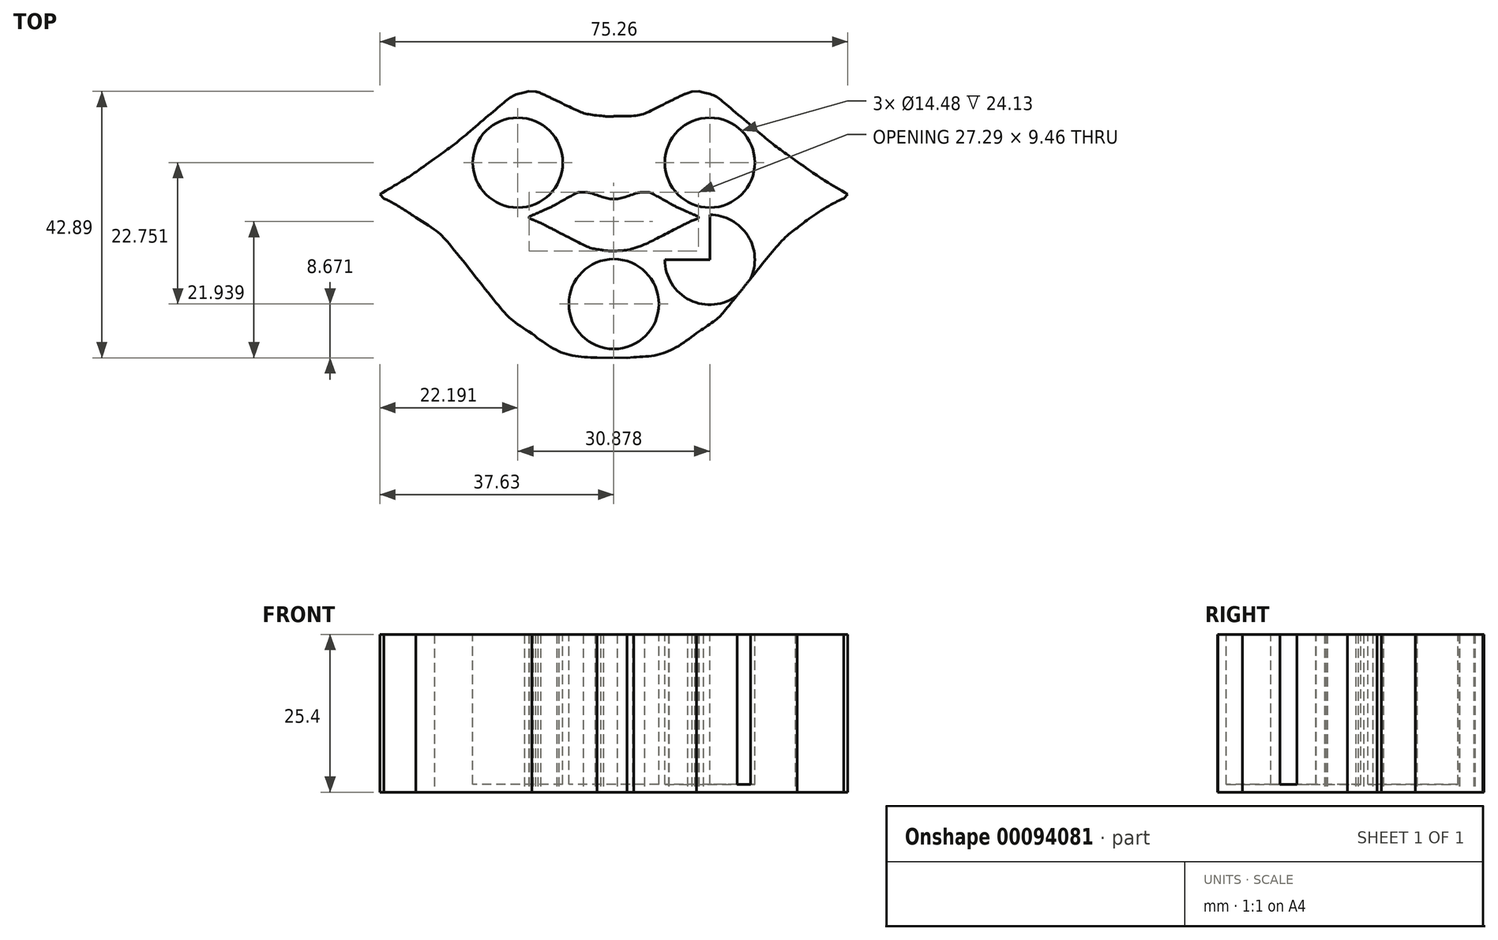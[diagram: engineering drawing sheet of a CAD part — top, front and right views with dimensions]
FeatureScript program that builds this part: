
annotation { "Feature Type Name" : "Feature", "Feature Type Description" : "" }
export const myFeature = defineFeature(function(context is Context, id is Id, definition is map)
    precondition{}
    {
        {
            var Q0;
            Q0=qCreatedBy(makeId("Top.planeOp"),FACE);
            var sketch = newSketch(context, id + "F0", { "sketchPlane" : qUnion([Q0])});
            skFitSpline(sketch, "E0", {"points": [v(-5.79, -23.43) * mm, v(-9.7, -22.6) * mm, v(-14.21, -19.9) * mm, v(-17.72, -16.3) * mm]});
            skFitSpline(sketch, "E1", {"points": [v(-17.72, -16.3) * mm, v(-19.37, -14.6) * mm, v(-19.96, -13.9) * mm, v(-22.42, -10.84) * mm]});
            skFitSpline(sketch, "E2", {"points": [v(-22.42, -10.84) * mm, v(-25.94, -6.44) * mm, v(-27.82, -4.4) * mm, v(-29.91, -2.76) * mm]});
            skFitSpline(sketch, "E3", {"points": [v(-29.91, -2.76) * mm, v(-31.51, -1.5) * mm, v(-35.93, 1.25) * mm, v(-37.43, 1.91) * mm]});
            skFitSpline(sketch, "E4", {"points": [v(-37.43, 1.91) * mm, v(-37.97, 2.15) * mm, v(-38.1, 2.27) * mm, v(-38.1, 2.52) * mm]});
            skFitSpline(sketch, "E5", {"points": [v(-38.1, 2.52) * mm, v(-38.1, 2.77) * mm, v(-37.87, 2.96) * mm, v(-36.73, 3.63) * mm]});
            skFitSpline(sketch, "E6", {"points": [v(-36.73, 3.63) * mm, v(-32.2, 6.28) * mm, v(-26.83, 10.13) * mm, v(-22.5, 13.82) * mm]});
            skFitSpline(sketch, "E7", {"points": [v(-22.5, 13.82) * mm, v(-19.29, 16.56) * mm, v(-18.61, 17.1) * mm, v(-17.4, 17.92) * mm]});
            skFitSpline(sketch, "E8", {"points": [v(-17.4, 17.92) * mm, v(-15.92, 18.91) * mm, v(-15.04, 19.3) * mm, v(-14.29, 19.3) * mm]});
            skFitSpline(sketch, "E9", {"points": [v(-14.37, 19.1) * mm, v(-15.97, 18.67) * mm, v(-17.57, 17.59) * mm, v(-21.4, 14.33) * mm]});
            skFitSpline(sketch, "E10", {"points": [v(-21.4, 14.33) * mm, v(-24.87, 11.4) * mm, v(-26.2, 10.35) * mm, v(-28.87, 8.44) * mm]});
            skFitSpline(sketch, "E11", {"points": [v(-28.87, 8.44) * mm, v(-32.22, 6.05) * mm, v(-33.92, 4.94) * mm, v(-37.63, 2.73) * mm]});
            skLineSegment(sketch, "E12", {"start": v(-14.29, 19.3) * mm, "end": v(-13.7, 19.28) * mm});
            skLineSegment(sketch, "E13", {"start": v(-13.7, 19.28) * mm, "end": v(-14.37, 19.1) * mm});
            skLineSegment(sketch, "E14", {"start": v(-14.37, 19.1) * mm, "end": v(-14.29, 19.3) * mm});
            skFitSpline(sketch, "E15", {"points": [v(-37.01, 2.05) * mm, v(-35.86, 1.5) * mm, v(-33.73, 0.24) * mm, v(-31.86, -1) * mm]});
            skFitSpline(sketch, "E16", {"points": [v(-31.86, -1) * mm, v(-28.39, -3.31) * mm, v(-26.8, -4.9) * mm, v(-22.17, -10.65) * mm]});
            skFitSpline(sketch, "E17", {"points": [v(-22.17, -10.65) * mm, v(-17.88, -15.97) * mm, v(-16.31, -17.55) * mm, v(-13.19, -19.7) * mm]});
            skFitSpline(sketch, "E18", {"points": [v(-13.19, -19.7) * mm, v(-9.72, -22.1) * mm, v(-6.52, -23.27) * mm, v(-2.68, -23.55) * mm]});
            skFitSpline(sketch, "E19", {"points": [v(-2.68, -23.55) * mm, v(-2.36, -23.58) * mm, v(-2.73, -23.6) * mm, v(-3.5, -23.6) * mm]});
            skFitSpline(sketch, "E20", {"points": [v(-3.5, -23.6) * mm, v(-4.3, -23.62) * mm, v(-5.28, -23.54) * mm, v(-5.79, -23.43) * mm]});
            skLineSegment(sketch, "E21", {"start": v(-37.63, 2.73) * mm, "end": v(-38, 2.52) * mm});
            skLineSegment(sketch, "E22", {"start": v(-38, 2.52) * mm, "end": v(-37.01, 2.05) * mm});
            skLineSegment(sketch, "E23", {"start": v(-37.01, 2.05) * mm, "end": v(-37.63, 2.73) * mm});
            skFitSpline(sketch, "E24", {"points": [v(3.19, -23.5) * mm, v(6.82, -23.15) * mm, v(9.98, -21.94) * mm, v(13.32, -19.62) * mm]});
            skFitSpline(sketch, "E25", {"points": [v(13.32, -19.62) * mm, v(16.41, -17.47) * mm, v(17.9, -15.94) * mm, v(22.64, -10.07) * mm]});
            skFitSpline(sketch, "E26", {"points": [v(22.64, -10.07) * mm, v(25.5, -6.52) * mm, v(27.9, -3.93) * mm, v(29.47, -2.7) * mm]});
            skFitSpline(sketch, "E27", {"points": [v(29.47, -2.7) * mm, v(31.47, -1.16) * mm, v(35.15, 1.17) * mm, v(37.01, 2.05) * mm]});
            skFitSpline(sketch, "E28", {"points": [v(37.63, 2.73) * mm, v(33.92, 4.94) * mm, v(32.57, 5.82) * mm, v(29.18, 8.22) * mm]});
            skFitSpline(sketch, "E29", {"points": [v(29.18, 8.22) * mm, v(26.56, 10.07) * mm, v(24.5, 11.69) * mm, v(21.79, 14) * mm]});
            skFitSpline(sketch, "E30", {"points": [v(21.79, 14) * mm, v(17.56, 17.62) * mm, v(16.07, 18.64) * mm, v(14.37, 19.1) * mm]});
            skLineSegment(sketch, "E31", {"start": v(37.01, 2.05) * mm, "end": v(38, 2.52) * mm});
            skLineSegment(sketch, "E32", {"start": v(38, 2.52) * mm, "end": v(37.63, 2.73) * mm});
            skLineSegment(sketch, "E33", {"start": v(37.63, 2.73) * mm, "end": v(37.01, 2.05) * mm});
            skFitSpline(sketch, "E34", {"points": [v(14.29, 19.3) * mm, v(15.04, 19.3) * mm, v(15.92, 18.91) * mm, v(17.4, 17.92) * mm]});
            skFitSpline(sketch, "E35", {"points": [v(17.4, 17.92) * mm, v(18.6, 17.1) * mm, v(19.26, 16.58) * mm, v(22.45, 13.86) * mm]});
            skFitSpline(sketch, "E36", {"points": [v(22.45, 13.86) * mm, v(23.53, 12.94) * mm, v(24.85, 11.85) * mm, v(25.37, 11.44) * mm]});
            skFitSpline(sketch, "E37", {"points": [v(25.37, 11.44) * mm, v(28.39, 9.04) * mm, v(33.59, 5.47) * mm, v(36.64, 3.68) * mm]});
            skFitSpline(sketch, "E38", {"points": [v(36.64, 3.68) * mm, v(37.86, 2.96) * mm, v(38.1, 2.77) * mm, v(38.1, 2.52) * mm]});
            skFitSpline(sketch, "E39", {"points": [v(38.1, 2.52) * mm, v(38.1, 2.27) * mm, v(37.97, 2.15) * mm, v(37.43, 1.91) * mm]});
            skFitSpline(sketch, "E40", {"points": [v(37.43, 1.91) * mm, v(35.93, 1.25) * mm, v(31.51, -1.5) * mm, v(29.91, -2.76) * mm]});
            skFitSpline(sketch, "E41", {"points": [v(29.91, -2.76) * mm, v(27.82, -4.4) * mm, v(25.94, -6.44) * mm, v(22.42, -10.84) * mm]});
            skFitSpline(sketch, "E42", {"points": [v(22.42, -10.84) * mm, v(19.96, -13.9) * mm, v(19.37, -14.6) * mm, v(17.72, -16.3) * mm]});
            skFitSpline(sketch, "E43", {"points": [v(17.72, -16.3) * mm, v(13.36, -20.77) * mm, v(7.7, -23.68) * mm, v(3.46, -23.63) * mm]});
            skLineSegment(sketch, "E44", {"start": v(14.37, 19.1) * mm, "end": v(13.7, 19.28) * mm});
            skLineSegment(sketch, "E45", {"start": v(13.7, 19.28) * mm, "end": v(14.29, 19.3) * mm});
            skLineSegment(sketch, "E46", {"start": v(14.29, 19.3) * mm, "end": v(14.37, 19.1) * mm});
            skFitSpline(sketch, "E47", {"points": [v(-2.1, -6.2) * mm, v(-3.6, -5.95) * mm, v(-5.15, -5.3) * mm, v(-9.5, -3.07) * mm]});
            skFitSpline(sketch, "E48", {"points": [v(-9.5, -3.07) * mm, v(-11.03, -2.28) * mm, v(-12.6, -1.53) * mm, v(-12.97, -1.4) * mm]});
            skFitSpline(sketch, "E49", {"points": [v(-12.97, -1.4) * mm, v(-13.33, -1.27) * mm, v(-13.63, -1.1) * mm, v(-13.63, -1.02) * mm]});
            skFitSpline(sketch, "E50", {"points": [v(-13.63, -1.02) * mm, v(-13.63, -0.95) * mm, v(-12.81, -0.52) * mm, v(-11.81, -0.09) * mm]});
            skFitSpline(sketch, "E51", {"points": [v(-11.81, -0.09) * mm, v(-10.81, 0.35) * mm, v(-9.48, 1) * mm, v(-8.85, 1.35) * mm]});
            skFitSpline(sketch, "E52", {"points": [v(-8.85, 1.35) * mm, v(-6.3, 2.79) * mm, v(-5.72, 3.03) * mm, v(-4.9, 3.04) * mm]});
            skFitSpline(sketch, "E53", {"points": [v(-4.9, 3.04) * mm, v(-4.4, 3.05) * mm, v(-3.75, 2.93) * mm, v(-3, 2.7) * mm]});
            skFitSpline(sketch, "E54", {"points": [v(-3, 2.7) * mm, v(-0.82, 2.02) * mm, v(0.82, 2.02) * mm, v(3, 2.7) * mm]});
            skFitSpline(sketch, "E55", {"points": [v(3, 2.7) * mm, v(3.75, 2.93) * mm, v(4.4, 3.05) * mm, v(4.9, 3.04) * mm]});
            skFitSpline(sketch, "E56", {"points": [v(4.9, 3.04) * mm, v(5.72, 3.03) * mm, v(6.3, 2.79) * mm, v(8.85, 1.35) * mm]});
            skFitSpline(sketch, "E57", {"points": [v(8.85, 1.35) * mm, v(9.48, 1) * mm, v(10.81, 0.35) * mm, v(11.81, -0.09) * mm]});
            skFitSpline(sketch, "E58", {"points": [v(11.81, -0.09) * mm, v(12.81, -0.52) * mm, v(13.63, -0.95) * mm, v(13.63, -1.02) * mm]});
            skFitSpline(sketch, "E59", {"points": [v(13.63, -1.02) * mm, v(13.63, -1.1) * mm, v(13.33, -1.27) * mm, v(12.97, -1.4) * mm]});
            skFitSpline(sketch, "E60", {"points": [v(12.97, -1.4) * mm, v(12.6, -1.53) * mm, v(11.1, -2.25) * mm, v(9.62, -3.01) * mm]});
            skFitSpline(sketch, "E61", {"points": [v(9.62, -3.01) * mm, v(6.47, -4.63) * mm, v(4.34, -5.6) * mm, v(3.19, -5.95) * mm]});
            skFitSpline(sketch, "E62", {"points": [v(3.19, -5.95) * mm, v(2.26, -6.23) * mm, v(-0.96, -6.38) * mm, v(-2.1, -6.2) * mm]});
            skLineSegment(sketch, "E63", {"start": v(3.46, -23.63) * mm, "end": v(2.1, -23.6) * mm});
            skLineSegment(sketch, "E64", {"start": v(2.1, -23.6) * mm, "end": v(3.19, -23.5) * mm});
            skLineSegment(sketch, "E65", {"start": v(3.19, -23.5) * mm, "end": v(3.46, -23.63) * mm});
            skFitSpline(sketch, "E66", {"points": [v(2.79, -5.72) * mm, v(4.05, -5.4) * mm, v(6.73, -4.18) * mm, v(10.4, -2.25) * mm]});
            skFitSpline(sketch, "E67", {"points": [v(10.4, -2.25) * mm, v(11.2, -1.83) * mm, v(12.13, -1.38) * mm, v(12.49, -1.25) * mm]});
            skFitSpline(sketch, "E68", {"points": [v(12.27, -0.64) * mm, v(11.26, -0.22) * mm, v(8.41, 1.2) * mm, v(6.94, 2.03) * mm]});
            skFitSpline(sketch, "E69", {"points": [v(6.94, 2.03) * mm, v(6.38, 2.34) * mm, v(5.64, 2.66) * mm, v(5.29, 2.74) * mm]});
            skFitSpline(sketch, "E70", {"points": [v(5.29, 2.74) * mm, v(4.7, 2.87) * mm, v(4.53, 2.84) * mm, v(3.19, 2.42) * mm]});
            skFitSpline(sketch, "E71", {"points": [v(3.19, 2.42) * mm, v(0.71, 1.65) * mm, v(-0.76, 1.67) * mm, v(-3.4, 2.5) * mm]});
            skFitSpline(sketch, "E72", {"points": [v(-3.4, 2.5) * mm, v(-4.53, 2.84) * mm, v(-4.71, 2.87) * mm, v(-5.29, 2.74) * mm]});
            skFitSpline(sketch, "E73", {"points": [v(-5.29, 2.74) * mm, v(-5.64, 2.66) * mm, v(-6.38, 2.34) * mm, v(-6.94, 2.03) * mm]});
            skFitSpline(sketch, "E74", {"points": [v(-6.94, 2.03) * mm, v(-8.4, 1.21) * mm, v(-11.26, -0.22) * mm, v(-12.26, -0.64) * mm]});
            skLineSegment(sketch, "E75", {"start": v(12.49, -1.25) * mm, "end": v(13.14, -1) * mm});
            skLineSegment(sketch, "E76", {"start": v(13.14, -1) * mm, "end": v(12.27, -0.64) * mm});
            skLineSegment(sketch, "E77", {"start": v(12.27, -0.64) * mm, "end": v(12.49, -1.25) * mm});
            skFitSpline(sketch, "E78", {"points": [v(-12.07, -1.43) * mm, v(-11.5, -1.66) * mm, v(-10.42, -2.2) * mm, v(-9.68, -2.6) * mm]});
            skFitSpline(sketch, "E79", {"points": [v(-9.68, -2.6) * mm, v(-8.03, -3.53) * mm, v(-4.52, -5.18) * mm, v(-3.45, -5.54) * mm]});
            skFitSpline(sketch, "E80", {"points": [v(-3.45, -5.54) * mm, v(-1.86, -6.08) * mm, v(1.03, -6.16) * mm, v(2.79, -5.72) * mm]});
            skLineSegment(sketch, "E81", {"start": v(-12.26, -0.64) * mm, "end": v(-13.12, -1) * mm});
            skLineSegment(sketch, "E82", {"start": v(-13.12, -1) * mm, "end": v(-12.07, -1.43) * mm});
            skLineSegment(sketch, "E83", {"start": v(-12.07, -1.43) * mm, "end": v(-12.26, -0.64) * mm});
            skFitSpline(sketch, "E84", {"points": [v(-1.66, 15.3) * mm, v(-4.2, 15.63) * mm, v(-5.72, 16.13) * mm, v(-9.17, 17.78) * mm]});
            skFitSpline(sketch, "E85", {"points": [v(-9.17, 17.78) * mm, v(-10.61, 18.47) * mm, v(-11.99, 19.09) * mm, v(-12.23, 19.16) * mm]});
            skFitSpline(sketch, "E86", {"points": [v(-12.23, 19.16) * mm, v(-12.66, 19.3) * mm, v(-12.65, 19.3) * mm, v(-12, 19.25) * mm]});
            skFitSpline(sketch, "E87", {"points": [v(-12, 19.25) * mm, v(-11.47, 19.22) * mm, v(-10.82, 18.96) * mm, v(-8.7, 17.92) * mm]});
            skFitSpline(sketch, "E88", {"points": [v(-8.7, 17.92) * mm, v(-4.8, 16.04) * mm, v(-3.13, 15.59) * mm, v(0.06, 15.6) * mm]});
            skFitSpline(sketch, "E89", {"points": [v(0.06, 15.6) * mm, v(3.18, 15.6) * mm, v(5.1, 16.12) * mm, v(8.92, 18) * mm]});
            skFitSpline(sketch, "E90", {"points": [v(8.92, 18) * mm, v(10.82, 18.93) * mm, v(11.55, 19.23) * mm, v(12.04, 19.26) * mm]});
            skFitSpline(sketch, "E91", {"points": [v(11.85, 19) * mm, v(11.4, 18.84) * mm, v(10.02, 18.2) * mm, v(8.8, 17.6) * mm]});
            skFitSpline(sketch, "E92", {"points": [v(8.8, 17.6) * mm, v(5.38, 15.9) * mm, v(3.44, 15.36) * mm, v(0.5, 15.29) * mm]});
            skFitSpline(sketch, "E93", {"points": [v(0.5, 15.29) * mm, v(-0.44, 15.26) * mm, v(-1.41, 15.27) * mm, v(-1.66, 15.3) * mm]});
            skLineSegment(sketch, "E94", {"start": v(12.04, 19.26) * mm, "end": v(12.68, 19.31) * mm});
            skLineSegment(sketch, "E95", {"start": v(12.68, 19.31) * mm, "end": v(11.85, 19) * mm});
            skLineSegment(sketch, "E96", {"start": v(11.85, 19) * mm, "end": v(12.04, 19.26) * mm});
            skLineSegment(sketch, "E97", {"start": v(-1.66, 15.3) * mm, "end": v(-1.66, 15.3) * mm});
            skLineSegment(sketch, "E98", {"start": v(-2.68, -23.55) * mm, "end": v(2.1, -23.6) * mm});
            skLineSegment(sketch, "E99", {"start": v(-14.29, 19.3) * mm, "end": v(-12, 19.25) * mm});
            skLineSegment(sketch, "E100", {"start": v(12.04, 19.26) * mm, "end": v(14.29, 19.3) * mm});
            skLineSegment(sketch, "E101", {"start": v(13.7, 19.28) * mm, "end": v(13.7, 19.28) * mm});
            skSolve(sketch);
        }
        {
            var Q0;
            {var subQ6=sQuery(id+"F0.wireOp",EDGE,"E9");Q0=makeQuery(id+"F0.imprint","IMPRINT",FACE,{"disambiguationData":[TD([[makeQuery(id+"F0.imprint","IMPRINT",EDGE,{"derivedFrom":subQ6}),1.0]])]});}
            extrude(context, id + "F1", {"entities" : qUnion([Q0]), "depth" : 25.4 * mm});
        }
        {
            var Q0;
            Q0=makeQuery(id+"F1.opExtrude","CAP_FACE",FACE,{"disambiguationData":[OSD([sQuery(id+"F0.wireOp",EDGE,"E9"),sQuery(id+"F0.wireOp",EDGE,"E10"),sQuery(id+"F0.wireOp",EDGE,"E11"),sQuery(id+"F0.wireOp",EDGE,"E13"),sQuery(id+"F0.wireOp",EDGE,"E15"),sQuery(id+"F0.wireOp",EDGE,"E16"),sQuery(id+"F0.wireOp",EDGE,"E17"),sQuery(id+"F0.wireOp",EDGE,"E18"),sQuery(id+"F0.wireOp",EDGE,"E23"),sQuery(id+"F0.wireOp",EDGE,"E24"),sQuery(id+"F0.wireOp",EDGE,"E25"),sQuery(id+"F0.wireOp",EDGE,"E26"),sQuery(id+"F0.wireOp",EDGE,"E27"),sQuery(id+"F0.wireOp",EDGE,"E28"),sQuery(id+"F0.wireOp",EDGE,"E29"),sQuery(id+"F0.wireOp",EDGE,"E30"),sQuery(id+"F0.wireOp",EDGE,"E33"),sQuery(id+"F0.wireOp",EDGE,"E44"),sQuery(id+"F0.wireOp",EDGE,"E47"),sQuery(id+"F0.wireOp",EDGE,"E48"),sQuery(id+"F0.wireOp",EDGE,"E49"),sQuery(id+"F0.wireOp",EDGE,"E50"),sQuery(id+"F0.wireOp",EDGE,"E51"),sQuery(id+"F0.wireOp",EDGE,"E52"),sQuery(id+"F0.wireOp",EDGE,"E53"),sQuery(id+"F0.wireOp",EDGE,"E54"),sQuery(id+"F0.wireOp",EDGE,"E55"),sQuery(id+"F0.wireOp",EDGE,"E56"),sQuery(id+"F0.wireOp",EDGE,"E57"),sQuery(id+"F0.wireOp",EDGE,"E58"),sQuery(id+"F0.wireOp",EDGE,"E59"),sQuery(id+"F0.wireOp",EDGE,"E60"),sQuery(id+"F0.wireOp",EDGE,"E61"),sQuery(id+"F0.wireOp",EDGE,"E62"),sQuery(id+"F0.wireOp",EDGE,"E64"),sQuery(id+"F0.wireOp",EDGE,"E84"),sQuery(id+"F0.wireOp",EDGE,"E85"),sQuery(id+"F0.wireOp",EDGE,"E86"),sQuery(id+"F0.wireOp",EDGE,"E91"),sQuery(id+"F0.wireOp",EDGE,"E92"),sQuery(id+"F0.wireOp",EDGE,"E93"),sQuery(id+"F0.wireOp",EDGE,"E95"),sQuery(id+"F0.wireOp",EDGE,"E98"),sQuery(id+"F0.wireOp",EDGE,"E99"),sQuery(id+"F0.wireOp",EDGE,"E100"),sQuery(id+"F0.wireOp",EDGE,"E101")])],"isStart":false});
            var sketch = newSketch(context, id + "F2", { "sketchPlane" : qUnion([Q0])});
            skLineSegment(sketch, "E102.bottom", {"start": v(-15.44, 7.81) * mm, "end": v(15.44, 7.81) * mm});
            skLineSegment(sketch, "E102.top", {"start": v(-15.44, -7.81) * mm, "end": v(15.44, -7.81) * mm});
            skLineSegment(sketch, "E102.left", {"start": v(-15.44, 7.81) * mm, "end": v(-15.44, -7.81) * mm});
            skLineSegment(sketch, "E102.right", {"start": v(15.44, 7.81) * mm, "end": v(15.44, -7.81) * mm});
            skLineSegment(sketch, "E103", {"start": v(0, 7.81) * mm, "end": v(0, -7.81) * mm, "construction": true});
            skLineSegment(sketch, "E104", {"start": v(-15.44, 0) * mm, "end": v(15.44, 0) * mm, "construction": true});
            skLineSegment(sketch, "E105", {"start": v(0, 7.81) * mm, "end": v(0, -14.94) * mm, "construction": true});
            skLineSegment(sketch, "E106", {"start": v(-53.07, 0) * mm, "end": v(49.2, 0) * mm, "construction": true});
            skCircle(sketch, "E107", {"center": v(-53.07, 0) * mm, "radius": 7.24 * mm});
            skCircle(sketch, "E108", {"center": v(-15.44, 7.81) * mm, "radius": 7.24 * mm});
            skCircle(sketch, "E109", {"center": v(15.44, 7.81) * mm, "radius": 7.24 * mm});
            skCircle(sketch, "E110", {"center": v(49.2, 0) * mm, "radius": 7.24 * mm});
            skCircle(sketch, "E111", {"center": v(0, -14.94) * mm, "radius": 7.24 * mm});
            skCircle(sketch, "E112", {"center": v(15.44, -7.81) * mm, "radius": 7.24 * mm});
            skCircle(sketch, "E113", {"center": v(-15.44, -7.81) * mm, "radius": 7.24 * mm});
            skCircle(sketch, "E114", {"center": v(0, 11.06) * mm, "radius": 7.24 * mm});
            skSolve(sketch);
        }
        {
            var Q0;
            Q0=makeQuery(id+"F2.imprint","IMPRINT",FACE,{"disambiguationData":[TD([[makeQuery(id+"F2.imprint","IMPRINT",EDGE,{"derivedFrom":sQuery(id+"F2.wireOp",EDGE,"E107")}),1.0]])]});
            var Q1;
            Q1=makeQuery(id+"F2.imprint","IMPRINT",FACE,{"disambiguationData":[TD([[makeQuery(id+"F2.imprint","IMPRINT",EDGE,{"derivedFrom":sQuery(id+"F2.wireOp",EDGE,"E110")}),1.0]])]});
            var Q2;
            {var subQ0=sQuery(id+"F2.wireOp",EDGE,"E102.left");var subQ1=sQuery(id+"F2.wireOp",EDGE,"E102.bottom");var subQ2=makeQuery(id+"F2.imprint","INTERSECT",VERTEX,{"derivedFrom":[subQ1,subQ0]});Q2=makeQuery(id+"F2.imprint","IMPRINT",FACE,{"disambiguationData":[TD([[makeQuery(id+"F2.imprint","IMPRINT",EDGE,{"disambiguationData":[TD([[subQ2,-1.0]])],"derivedFrom":subQ1}),1.0]])]});}
            var Q3;
            {var subQ0=sQuery(id+"F2.wireOp",EDGE,"E102.left");var subQ1=sQuery(id+"F2.wireOp",EDGE,"E102.bottom");var subQ2=makeQuery(id+"F2.imprint","INTERSECT",VERTEX,{"derivedFrom":[subQ1,subQ0]});Q3=makeQuery(id+"F2.imprint","IMPRINT",FACE,{"disambiguationData":[TD([[makeQuery(id+"F2.imprint","IMPRINT",EDGE,{"disambiguationData":[TD([[subQ2,-1.0]])],"derivedFrom":subQ1}),-1.0]])]});}
            var Q4;
            {var subQ0=sQuery(id+"F2.wireOp",EDGE,"E102.right");var subQ1=sQuery(id+"F2.wireOp",EDGE,"E102.bottom");var subQ2=makeQuery(id+"F2.imprint","INTERSECT",VERTEX,{"derivedFrom":[subQ1,subQ0]});Q4=makeQuery(id+"F2.imprint","IMPRINT",FACE,{"disambiguationData":[TD([[makeQuery(id+"F2.imprint","IMPRINT",EDGE,{"disambiguationData":[TD([[subQ2,1.0]])],"derivedFrom":subQ1}),-1.0]])]});}
            var Q5;
            {var subQ0=sQuery(id+"F2.wireOp",EDGE,"E102.right");var subQ1=sQuery(id+"F2.wireOp",EDGE,"E102.bottom");var subQ2=makeQuery(id+"F2.imprint","INTERSECT",VERTEX,{"derivedFrom":[subQ1,subQ0]});Q5=makeQuery(id+"F2.imprint","IMPRINT",FACE,{"disambiguationData":[TD([[makeQuery(id+"F2.imprint","IMPRINT",EDGE,{"disambiguationData":[TD([[subQ2,1.0]])],"derivedFrom":subQ1}),1.0]])]});}
            var Q6;
            {var subQ0=sQuery(id+"F2.wireOp",EDGE,"E111");var subQ1=sQuery(id+"F2.wireOp",EDGE,"E102.top");var subQ2=makeQuery(id+"F2.imprint","INTERSECT",VERTEX,{"disambiguationData":[OD(0.0)],"derivedFrom":[subQ1,subQ0]});Q6=makeQuery(id+"F2.imprint","IMPRINT",FACE,{"disambiguationData":[TD([[makeQuery(id+"F2.imprint","IMPRINT",EDGE,{"disambiguationData":[TD([[subQ2,-1.0]])],"derivedFrom":subQ1}),1.0]])]});}
            var Q7;
            {var subQ0=sQuery(id+"F2.wireOp",EDGE,"E111");var subQ1=sQuery(id+"F2.wireOp",EDGE,"E102.top");var subQ2=makeQuery(id+"F2.imprint","INTERSECT",VERTEX,{"disambiguationData":[OD(0.0)],"derivedFrom":[subQ1,subQ0]});Q7=makeQuery(id+"F2.imprint","IMPRINT",FACE,{"disambiguationData":[TD([[makeQuery(id+"F2.imprint","IMPRINT",EDGE,{"disambiguationData":[TD([[subQ2,-1.0]])],"derivedFrom":subQ1}),-1.0]])]});}
            var Q8;
            {var subQ0=sQuery(id+"F2.wireOp",EDGE,"E112");var subQ1=makeQuery(id+"F1.opExtrude","CAP_EDGE",EDGE,{"disambiguationData":[OSD([sQuery(id+"F0.wireOp",EDGE,"E25")])],"isStart":false});var subQ2=makeQuery(id+"F2.imprint","INTERSECT",VERTEX,{"disambiguationData":[OD(0.0)],"derivedFrom":[subQ1,subQ0]});Q8=makeQuery(id+"F2.imprint","IMPRINT",FACE,{"disambiguationData":[TD([[makeQuery(id+"F2.imprint","IMPRINT",EDGE,{"disambiguationData":[TD([[subQ2,-1.0]])],"derivedFrom":subQ0}),1.0]])]});}
            var Q9;
            {var subQ0=sQuery(id+"F2.wireOp",EDGE,"E113");var subQ1=makeQuery(id+"F1.opExtrude","CAP_EDGE",EDGE,{"disambiguationData":[OSD([sQuery(id+"F0.wireOp",EDGE,"E17")])],"isStart":false});var subQ2=makeQuery(id+"F2.imprint","INTERSECT",VERTEX,{"disambiguationData":[OD(0.0)],"derivedFrom":[subQ1,subQ0]});Q9=makeQuery(id+"F2.imprint","IMPRINT",FACE,{"disambiguationData":[TD([[makeQuery(id+"F2.imprint","IMPRINT",EDGE,{"disambiguationData":[TD([[subQ2,-1.0]])],"derivedFrom":subQ0}),1.0]])]});}
            var Q10;
            {var subQ5=makeQuery(id+"F1.opExtrude","CAP_EDGE",EDGE,{"disambiguationData":[OSD([sQuery(id+"F0.wireOp",EDGE,"E93")])],"isStart":false});Q10=makeQuery(id+"F2.imprint","IMPRINT",FACE,{"disambiguationData":[TD([[makeQuery(id+"F2.imprint","IMPRINT",EDGE,{"derivedFrom":subQ5}),-1.0]])]});}
            var Q11;
            {var subQ5=makeQuery(id+"F1.opExtrude","CAP_EDGE",EDGE,{"disambiguationData":[OSD([sQuery(id+"F0.wireOp",EDGE,"E59")])],"isStart":false});Q11=makeQuery(id+"F2.imprint","IMPRINT",FACE,{"disambiguationData":[TD([[makeQuery(id+"F2.imprint","IMPRINT",EDGE,{"derivedFrom":subQ5}),-1.0]])]});}
            var Q12;
            {var subQ5=makeQuery(id+"F1.opExtrude","CAP_EDGE",EDGE,{"disambiguationData":[OSD([sQuery(id+"F0.wireOp",EDGE,"E49")])],"isStart":false});Q12=makeQuery(id+"F2.imprint","IMPRINT",FACE,{"disambiguationData":[TD([[makeQuery(id+"F2.imprint","IMPRINT",EDGE,{"derivedFrom":subQ5}),-1.0]])]});}
            var Q13;
            {var subQ1=makeQuery(id+"F1.opExtrude","CAP_EDGE",EDGE,{"disambiguationData":[OSD([sQuery(id+"F0.wireOp",EDGE,"E47")])],"isStart":false});Q13=makeQuery(id+"F2.imprint","IMPRINT",FACE,{"disambiguationData":[TD([[makeQuery(id+"F2.imprint","IMPRINT",EDGE,{"derivedFrom":subQ1}),-1.0]])]});}
            extrude(context, id + "F3", {"entities" : qUnion([Q0, Q1, Q2, Q3, Q4, Q5, Q6, Q7, Q8, Q9, Q10, Q11, Q12, Q13]), "operationType" : NewBodyOperationType.REMOVE, "oppositeDirection" : true, "depth" : 24.13 * mm});
        }
    });
